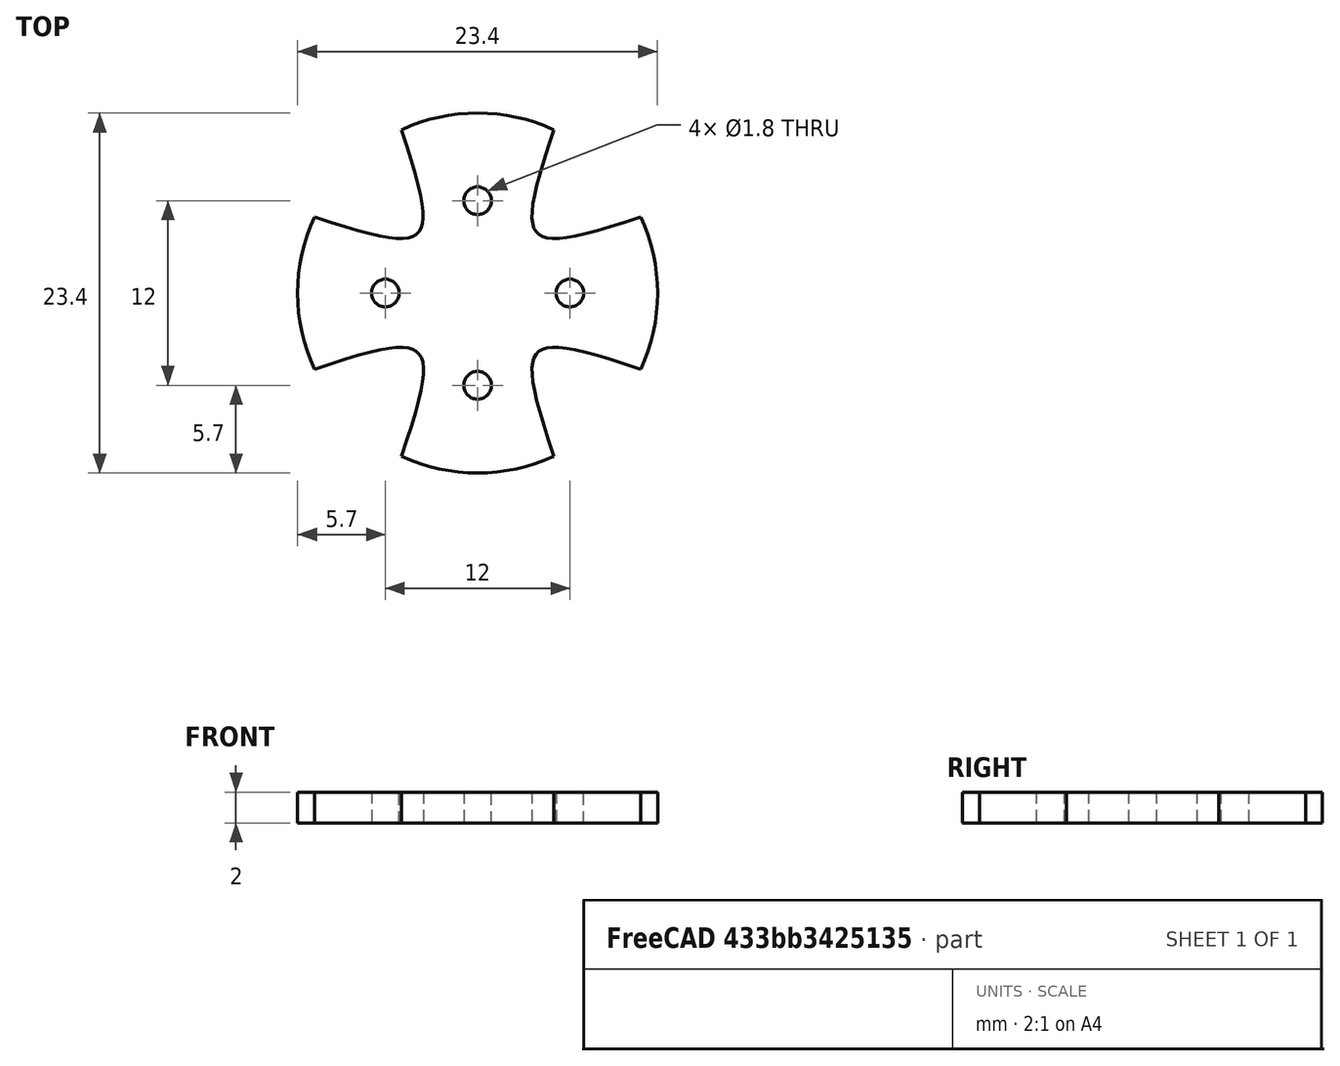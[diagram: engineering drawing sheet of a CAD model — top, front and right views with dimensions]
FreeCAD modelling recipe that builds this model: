
FCSTD DOCUMENT  (FreeCAD 0.19R0.19.2)
Label: boatMoterHolder008
License: All rights reserved
LicenseURL: http://en.wikipedia.org/wiki/All_rights_reserved
objects: Sketcher::SketchObject×2, Part::Extrusion×1
note: 3 computed .brp shape members not serialized (recipe doc carries the construction recipe); baked Part::Feature solids carry a one-line shape summary decoded from their .brp

FEATURE [Sketcher::SketchObject] Sketch
  FullyConstrained = true
  sketch-geometry (44):
    g0: Circle CenterX=-6 CenterY=0 CenterZ=0 NormalX=0 NormalY=0 NormalZ=1 AngleXU=0 Radius=0.9
    g1: Circle CenterX=0 CenterY=6 CenterZ=0 NormalX=0 NormalY=0 NormalZ=1 AngleXU=0 Radius=0.9
    g2: Circle CenterX=6 CenterY=0 CenterZ=0 NormalX=0 NormalY=0 NormalZ=1 AngleXU=0 Radius=0.9
    g3: Circle CenterX=0 CenterY=-6 CenterZ=0 NormalX=0 NormalY=0 NormalZ=1 AngleXU=0 Radius=0.9
    g4-g8: Circle x5 (B-spline internal-alignment scaffolding for g9; pole/knot coordinates omitted)
    g9: BSplineCurve PolesCount=5 KnotsCount=3 Degree=3 IsPeriodic=0
    g10: GeomPoint X=-4.94974 Y=10.6066 Z=0
    g11: GeomPoint X=-3.88908 Y=3.88909 Z=0
    g12: GeomPoint X=-10.6066 Y=4.94975 Z=0
    g13-g17: Circle x5 (B-spline internal-alignment scaffolding for g18; pole/knot coordinates omitted)
    g18: BSplineCurve PolesCount=5 KnotsCount=3 Degree=3 IsPeriodic=0
    g19: GeomPoint X=-10.6066 Y=-4.94974 Z=0
    g20: GeomPoint X=-3.88212 Y=-3.88197 Z=0
    g21: GeomPoint X=-4.94053 Y=-10.6109 Z=0
    g22-g26: Circle x5 (B-spline internal-alignment scaffolding for g27; pole/knot coordinates omitted)
    g27: BSplineCurve PolesCount=5 KnotsCount=3 Degree=3 IsPeriodic=0
    g28: GeomPoint X=4.94975 Y=-10.6066 Z=0
    g29: GeomPoint X=3.8852 Y=-3.88525 Z=0
    g30: GeomPoint X=10.603 Y=-4.95737 Z=0
    g31-g35: Circle x5 (B-spline internal-alignment scaffolding for g36; pole/knot coordinates omitted)
    g36: BSplineCurve PolesCount=5 KnotsCount=3 Degree=3 IsPeriodic=0
    g37: GeomPoint X=10.6066 Y=4.94975 Z=0
    g38: GeomPoint X=3.8891 Y=3.88908 Z=0
    g39: GeomPoint X=4.94975 Y=10.6066 Z=0
    g40: ArcOfCircle CenterX=0 CenterY=0 CenterZ=0 NormalX=0 NormalY=0 NormalZ=1 AngleXU=0 Radius=11.7047 StartAngle=1.13417 EndAngle=2.00742
    g41: ArcOfCircle CenterX=0 CenterY=0 CenterZ=0 NormalX=0 NormalY=0 NormalZ=1 AngleXU=0 Radius=11.7047 StartAngle=5.84584 EndAngle=6.71981
    g42: ArcOfCircle CenterX=0 CenterY=0 CenterZ=0 NormalX=0 NormalY=0 NormalZ=1 AngleXU=0 Radius=11.7047 StartAngle=4.27663 EndAngle=5.14902
    g43: ArcOfCircle CenterX=0 CenterY=0 CenterZ=0 NormalX=0 NormalY=0 NormalZ=1 AngleXU=0 Radius=11.7047 StartAngle=2.70497 EndAngle=3.57822
  constraints (50):
    c: Block(g1)
    c: Block(g2)
    c: Block(g3)
    c: Block(g0)
    c: Weight(g4) = 1
    c: Equal(g4, g5-g8) x4
    c: InternalAlignment(g4-g8 -> g9) x5
    c: InternalAlignment(g10,g9)
    c: InternalAlignment(g11,g9)
    c: InternalAlignment(g12,g9)
    c: Weight(g13) = 1
    c: Equal(g13, g14-g17) x4
    c: InternalAlignment(g13-g17 -> g18) x5
    c: InternalAlignment(g19,g18)
    c: InternalAlignment(g20,g18)
    c: InternalAlignment(g21,g18)
    c: Weight(g22) = 1
    c: Equal(g22,g24)
    c: Equal(g22,g25)
    c: Equal(g22,g26)
    c: InternalAlignment(g22-g26 -> g27) x5
    c: InternalAlignment(g28,g27)
    c: InternalAlignment(g29,g27)
    c: InternalAlignment(g30,g27)
    c: Weight(g31) = 1
    c: Equal(g31, g32-g35) x4
    c: InternalAlignment(g31-g35 -> g36) x5
    c: InternalAlignment(g37,g36)
    c: InternalAlignment(g38,g36)
    c: InternalAlignment(g39,g36)
    c: Coincident(g40,g-1)
    c: Coincident(g40,g9)
    c: Coincident(g40,g36)
    c: Coincident(g41,g40)
    c: Coincident(g41,g36)
    c: Coincident(g41,g27)
    c: Coincident(g42,g40)
    c: Coincident(g42,g27)
    c: Coincident(g42,g18)
    c: Coincident(g43,g40)
    c: Coincident(g43,g18)
    c: Coincident(g43,g9)
    c: Block(g41)
    c: Block(g40)
    c: Block(g43)
    c: Block(g42)
    c: Block(g36)
    c: Block(g9)
    c: Block(g27)
    c: Block(g18)
FEATURE [Part::Extrusion] Extrude
  Base = -> Sketch
  Dir = (0,0,1)
  DirMode = 2
  FaceMakerClass = Part::FaceMakerBullseye
  LengthFwd = 2
  LengthRev = 0
  Solid = true
  Symmetric = false
FEATURE [Sketcher::SketchObject] Sketch001
  FullyConstrained = false
  sketch-geometry (60):
    g0: Circle CenterX=-6 CenterY=0 CenterZ=0 NormalX=0 NormalY=0 NormalZ=1 AngleXU=0 Radius=0.9
    g1: Circle CenterX=0 CenterY=6 CenterZ=0 NormalX=0 NormalY=0 NormalZ=1 AngleXU=0 Radius=0.9
    g2: Circle CenterX=6 CenterY=0 CenterZ=0 NormalX=0 NormalY=0 NormalZ=1 AngleXU=0 Radius=0.9
    g3: Circle CenterX=-0.014714 CenterY=-6 CenterZ=0 NormalX=0 NormalY=0 NormalZ=1 AngleXU=0 Radius=0.9
    g4-g8: Circle x5 (B-spline internal-alignment scaffolding for g9; pole/knot coordinates omitted)
    g9: BSplineCurve PolesCount=5 KnotsCount=3 Degree=3 IsPeriodic=0
    g10: GeomPoint X=-4.94974 Y=10.6066 Z=0
    g11: GeomPoint X=-3.88908 Y=3.88909 Z=0
    g12: GeomPoint X=-10.6066 Y=4.94975 Z=0
    g13-g17: Circle x5 (B-spline internal-alignment scaffolding for g18; pole/knot coordinates omitted)
    g18: BSplineCurve PolesCount=5 KnotsCount=3 Degree=3 IsPeriodic=0
    g19: GeomPoint X=-10.6066 Y=-4.94974 Z=0
    g20: GeomPoint X=-3.88212 Y=-3.88197 Z=0
    g21: GeomPoint X=-4.94053 Y=-10.6109 Z=0
    g22-g26: Circle x5 (B-spline internal-alignment scaffolding for g27; pole/knot coordinates omitted)
    g27: BSplineCurve PolesCount=5 KnotsCount=3 Degree=3 IsPeriodic=0
    g28: GeomPoint X=4.94975 Y=-10.6066 Z=0
    g29: GeomPoint X=3.8852 Y=-3.88525 Z=0
    g30: GeomPoint X=10.603 Y=-4.95737 Z=0
    g31-g35: Circle x5 (B-spline internal-alignment scaffolding for g36; pole/knot coordinates omitted)
    g36: BSplineCurve PolesCount=5 KnotsCount=3 Degree=3 IsPeriodic=0
    g37: GeomPoint X=10.6066 Y=4.94975 Z=0
    g38: GeomPoint X=3.8891 Y=3.88908 Z=0
    g39: GeomPoint X=4.94975 Y=10.6066 Z=0
    g40: ArcOfCircle CenterX=0 CenterY=0 CenterZ=0 NormalX=0 NormalY=0 NormalZ=1 AngleXU=0 Radius=11.7047 StartAngle=1.13417 EndAngle=2.00742
    g41: ArcOfCircle CenterX=0 CenterY=0 CenterZ=0 NormalX=0 NormalY=0 NormalZ=1 AngleXU=0 Radius=11.7047 StartAngle=5.84584 EndAngle=6.71981
    g42: ArcOfCircle CenterX=0 CenterY=0 CenterZ=0 NormalX=0 NormalY=0 NormalZ=1 AngleXU=0 Radius=11.7047 StartAngle=4.27663 EndAngle=5.14902
    g43: ArcOfCircle CenterX=0 CenterY=0 CenterZ=0 NormalX=0 NormalY=0 NormalZ=1 AngleXU=0 Radius=11.7047 StartAngle=2.70497 EndAngle=3.57822
    g44: LineSegment StartX=0 StartY=22.4 StartZ=0 EndX=0.8 EndY=22.4 EndZ=0
    g45: LineSegment StartX=0 StartY=22.4 StartZ=0 EndX=-0.8 EndY=22.4 EndZ=0
    g46: LineSegment StartX=-0.014714 StartY=-22.4 StartZ=0 EndX=-0.814714 EndY=-22.4 EndZ=0
    g47: LineSegment StartX=0.010719 StartY=-22.4 StartZ=0 EndX=0.810719 EndY=-22.4 EndZ=0
    g48: LineSegment StartX=22.4 StartY=0 StartZ=0 EndX=22.4 EndY=0.8 EndZ=0
    g49: LineSegment StartX=22.4 StartY=0 StartZ=0 EndX=22.4 EndY=-0.8 EndZ=0
    g50: LineSegment StartX=22.4 StartY=-0.8 StartZ=0 EndX=11.6773 EndY=-0.8 EndZ=0
    g51: LineSegment StartX=22.4 StartY=0.8 StartZ=0 EndX=11.6773 EndY=0.8 EndZ=0
    g52: LineSegment StartX=0.8 StartY=22.4 StartZ=0 EndX=0.8 EndY=11.6773 EndZ=0
    g53: LineSegment StartX=-0.8 StartY=22.4 StartZ=0 EndX=-0.8 EndY=11.6773 EndZ=0
    g54: LineSegment StartX=-22.4 StartY=0.8 StartZ=0 EndX=-11.6773 EndY=0.8 EndZ=0
    g55: LineSegment StartX=-22.4 StartY=-0.8 StartZ=0 EndX=-11.6773 EndY=-0.8 EndZ=0
    g56: LineSegment StartX=-0.014714 StartY=-6 StartZ=0 EndX=-0.014714 EndY=-22.4 EndZ=0
    g57: LineSegment StartX=0.810719 StartY=-22.4 StartZ=0 EndX=0.810719 EndY=-11.6766 EndZ=0
    g58: LineSegment StartX=-0.814714 StartY=-22.4 StartZ=0 EndX=-0.814714 EndY=-11.6763 EndZ=0
    g59: LineSegment StartX=-22.4 StartY=0.8 StartZ=0 EndX=-22.4 EndY=-0.8 EndZ=0
  constraints (98):
    c: Block(g1)
    c: Block(g2)
    c: Block(g3)
    c: Block(g0)
    c: Weight(g4) = 1
    c: Equal(g4, g5-g8) x4
    c: InternalAlignment(g4-g8 -> g9) x5
    c: InternalAlignment(g10,g9)
    c: InternalAlignment(g11,g9)
    c: InternalAlignment(g12,g9)
    c: Weight(g13) = 1
    c: Equal(g13, g14-g17) x4
    c: InternalAlignment(g13-g17 -> g18) x5
    c: InternalAlignment(g19,g18)
    c: InternalAlignment(g20,g18)
    c: InternalAlignment(g21,g18)
    c: Weight(g22) = 1
    c: Equal(g22,g24)
    c: Equal(g22,g25)
    c: Equal(g22,g26)
    c: InternalAlignment(g22-g26 -> g27) x5
    c: InternalAlignment(g28,g27)
    c: InternalAlignment(g29,g27)
    c: InternalAlignment(g30,g27)
    c: Weight(g31) = 1
    c: Equal(g31, g32-g35) x4
    c: InternalAlignment(g31-g35 -> g36) x5
    c: InternalAlignment(g37,g36)
    c: InternalAlignment(g38,g36)
    c: InternalAlignment(g39,g36)
    c: Coincident(g40,g-1)
    c: Coincident(g40,g9)
    c: Coincident(g40,g36)
    c: Coincident(g41,g40)
    c: Coincident(g41,g36)
    c: Coincident(g41,g27)
    c: Coincident(g42,g40)
    c: Coincident(g42,g27)
    c: Coincident(g42,g18)
    c: Coincident(g43,g40)
    c: Coincident(g43,g18)
    c: Coincident(g43,g9)
    c: Block(g41)
    c: Block(g40)
    c: Block(g43)
    c: Block(g42)
    c: Block(g36)
    c: Block(g9)
    c: Block(g27)
    c: Block(g18)
    c: Horizontal(g44)
    c: Distance(g44) = 0.8
    c: Horizontal(g45)
    c: Distance(g45) = 0.8
    c: Horizontal(g46)
    c: Distance(g46) = 0.8
    c: Horizontal(g47)
    c: Distance(g47) = 0.8
    c: Vertical(g48)
    c: Distance(g48) = 0.8
    c: Vertical(g49)
    c: Distance(g49) = 0.8
    c: Coincident(g50,g49)
    c: PointOnObject(g50,g41)
    c: Horizontal(g50)
    c: Coincident(g51,g48)
    c: Horizontal(g51)
    c: Coincident(g52,g44)
    c: PointOnObject(g52,g40)
    c: Vertical(g52)
    c: Coincident(g53,g45)
    c: PointOnObject(g53,g40)
    c: Vertical(g53)
    c: PointOnObject(g54,g43)
    c: Horizontal(g54)
    c: PointOnObject(g55,g43)
    c: Horizontal(g55)
    c: Block(g47)
    c: Block(g46)
    c: Block(g55)
    c: Block(g54)
    c: Block(g53)
    c: Block(g52)
    c: Block(g51)
    c: Block(g50)
    c: Coincident(g56,g3)
    c: Coincident(g56,g46)
    c: Vertical(g56)
    c: Coincident(g57,g47)
    c: PointOnObject(g57,g42)
    c: Vertical(g57)
    c: Coincident(g58,g46)
    c: PointOnObject(g58,g42)
    c: Vertical(g58)
    c: Coincident(g59,g54)
    c: Coincident(g59,g55)
    c: Vertical(g59)
    c: Distance(g59) = 1.6
